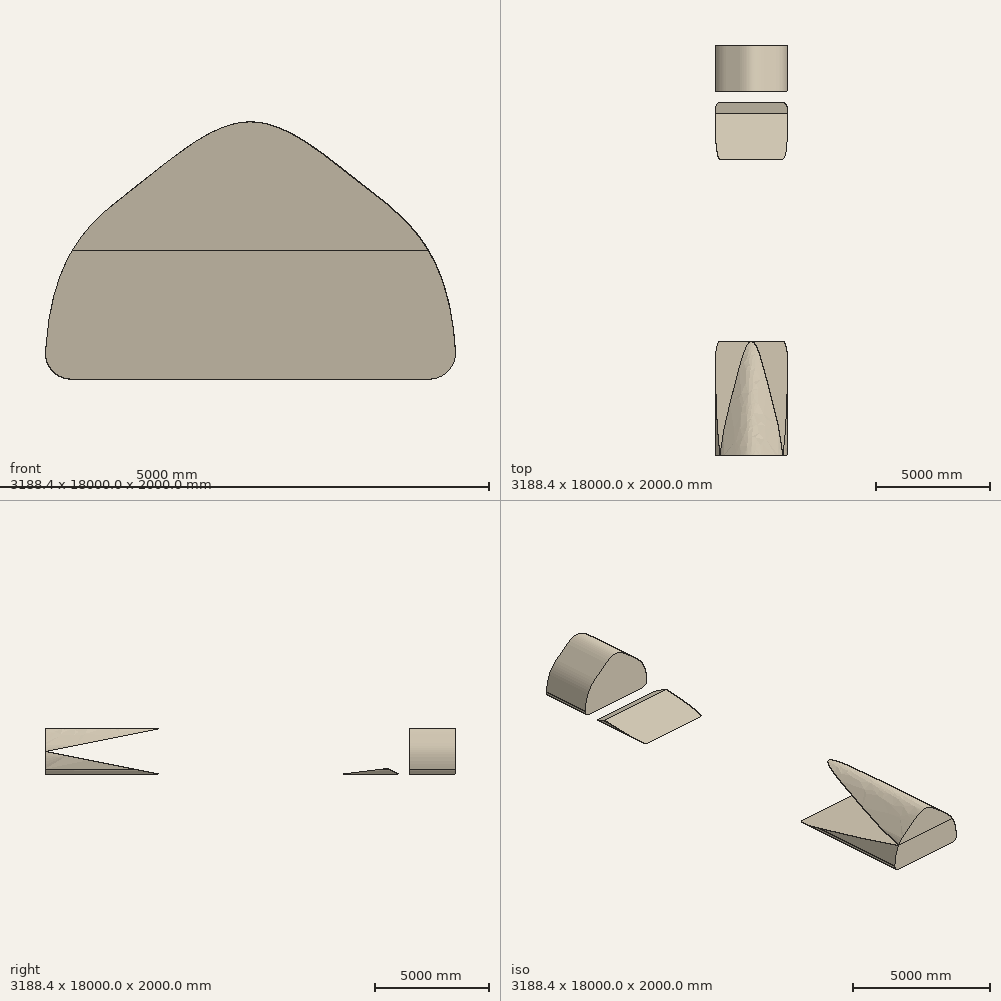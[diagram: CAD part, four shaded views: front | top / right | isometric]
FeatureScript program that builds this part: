
annotation { "Feature Type Name" : "Feature", "Feature Type Description" : "" }
export const myFeature = defineFeature(function(context is Context, id is Id, definition is map)
    precondition{}
    {
        {
            var Q0;
            Q0=qCreatedBy(makeId("Right.planeOp"),FACE);
            var sketch = newSketch(context, id + "F0", { "sketchPlane" : qUnion([Q0])});
            skLineSegment(sketch, "E0.bottom", {"start": v(-4000, 1000) * mm, "end": v(4000, 1000) * mm});
            skLineSegment(sketch, "E0.top", {"start": v(-4000, -1000) * mm, "end": v(4000, -1000) * mm});
            skLineSegment(sketch, "E0.left", {"start": v(-4000, 1000) * mm, "end": v(-4000, -1000) * mm});
            skLineSegment(sketch, "E0.right", {"start": v(4000, 1000) * mm, "end": v(4000, -1000) * mm});
            skPoint(sketch, "E0.middle", {"position": v(0, 0) * mm});
            skLineSegment(sketch, "E1", {"start": v(-4000, -1000) * mm, "end": v(-9000, 0) * mm});
            skLineSegment(sketch, "E2", {"start": v(-9000, 0) * mm, "end": v(-4000, 1000) * mm});
            skLineSegment(sketch, "E3", {"start": v(4000, 1000) * mm, "end": v(6000, 1000) * mm});
            skLineSegment(sketch, "E4", {"start": v(6000, 1000) * mm, "end": v(6000, -750) * mm});
            skLineSegment(sketch, "E5", {"start": v(4000, -1000) * mm, "end": v(6000, -750) * mm});
            skLineSegment(sketch, "E6", {"start": v(6000, 1000) * mm, "end": v(7000, 1000) * mm});
            skLineSegment(sketch, "E7", {"start": v(7000, 1000) * mm, "end": v(7000, -1250) * mm});
            skLineSegment(sketch, "E8", {"start": v(7000, -1250) * mm, "end": v(6000, -750) * mm});
            skLineSegment(sketch, "E9", {"start": v(7000, 1000) * mm, "end": v(8000, 1000) * mm});
            skSolve(sketch);
        }
        {
            var Q0;
            Q0=qCreatedBy(makeId("Front.planeOp"),FACE);
            var sketch = newSketch(context, id + "F1", { "sketchPlane" : qUnion([Q0])});
            skLineSegment(sketch, "E10.top", {"start": v(-1394.2, -1000) * mm, "end": v(1394.2, -1000) * mm});
            skPoint(sketch, "E10.middle", {"position": v(0, 0) * mm});
            skFitSpline(sketch, "E11", {"points": [v(-1600, -1000) * mm, v(-848, 530) * mm, v(0, 1000) * mm, v(848, 530) * mm, v(1600, -1000) * mm], "startDerivative": vector(0, 10524.75) * mm, "endDerivative": vector(0, -10524.75) * mm});
            skArc(sketch, "E12.filletArc", {"start": v(-1593.82, -787.83) * mm, "mid": v(-1539.85, -937.05) * mm, "end": v(-1394.2, -1000) * mm});
            skArc(sketch, "E13.filletArc", {"start": v(1394.2, -1000) * mm, "mid": v(1539.85, -937.05) * mm, "end": v(1593.82, -787.83) * mm});
            skSolve(sketch);
        }
        {
            var Q0;
            Q0 = qSketchRegion(id + "F1", true);
            extrude(context, id + "F2", {"entities" : qUnion([Q0]), "endBound" : BoundingType.SYMMETRIC, "depth" : 18000 * mm});
        }
        {
            var Q0;
            Q0 = qSketchRegion(id + "F0", true);
            extrude(context, id + "F3", {"entities" : qUnion([Q0]), "operationType" : NewBodyOperationType.REMOVE, "endBound" : BoundingType.SYMMETRIC, "oppositeDirection" : true, "depth" : 5000 * mm});
        }
    });
